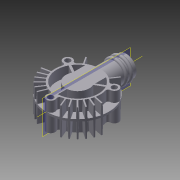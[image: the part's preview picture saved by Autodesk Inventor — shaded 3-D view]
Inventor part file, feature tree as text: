
AUTODESK INVENTOR PART (.ipt)
format: ipt  version: 2014 (Build 180170000, 170)  size: 2,437,632 bytes
history: native  units: in
note: dims shown in document units (in); Inventor stores cm internally (conversion verified against a paired STEP export)
features: sketch x24, extrude x21, pattern_circular x9, plane x4, draft x4, mirror x3, fillet x2, hole x2, revolve x2, other x1, thread x1
ambient origin geometry x8: Origin, YZ Plane, XZ Plane, XY Plane, X Axis, Y Axis, Z Axis, Center Point
bodies: Solid1 (feature_tree)
feature tree (73):
  extrude  "Extrusion1"  Depth=0.05in TaperAngle=0.0deg
  extrude  "Extrusion2"  Depth=1.08in
  extrude  "Extrusion3"  Depth=0.5in
  pattern_circular  "Circular Pattern1"  Count=3 Angle=360.0deg
  plane  "Work Plane2"
  extrude  "Extrusion17"  Depth=0.25in TaperAngle=0.0deg
  extrude  "Extrusion20"  Depth=0.25in
  draft  "FaceDraft5"
  draft  "FaceDraft6"
  fillet  "Fillet6"  Radius=0.125in
  pattern_circular  "Circular Pattern7"  Count=3 Angle=360.0deg
  extrude  "Extrusion21"  Depth=0.25in TaperAngle=360.0deg
  pattern_circular  "Circular Pattern8"  [2 undecoded]
  extrude  "Extrusion22"  Depth=0.25in
  draft  "FaceDraft7"
  draft  "FaceDraft8"
  fillet  "Fillet7"  Radius=0.125in
  pattern_circular  "Circular Pattern9"  [2 undecoded]
  extrude  "Extrusion23"  Depth=0.25in
  pattern_circular  "Circular Pattern10"  [2 undecoded]
  hole  "Hole1"  [1 undecoded]
  pattern_circular  "Circular Pattern11"  [2 undecoded]
  extrude  "Extrusion24"  Depth=0.25in
  plane  "Work Plane5"
  extrude  "Extrusion25"  Depth=0.25in TaperAngle=0.0deg
  hole  "Hole2"  [1 undecoded]
  other  "Work Axis1"
  revolve  "Revolution2"  [1 undecoded]
  pattern_circular  "Circular Pattern2"  [2 undecoded]
  extrude  "Extrusion5"  Depth=0.25in TaperAngle=360.0deg
  extrude  "Extrusion6"  Depth=0.25in
  mirror  "Mirror1"
  mirror  "Mirror2"
  extrude  "Extrusion7"  Depth=0.25in
  extrude  "Extrusion8"  Depth=0.25in TaperAngle=0.0deg
  extrude  "Extrusion9"  Depth=0.25in TaperAngle=360.0deg
  pattern_circular  "Circular Pattern3"  [2 undecoded]
  mirror  "Mirror3"
  extrude  "Extrusion10"  Depth=0.25in
  pattern_circular  "Circular Pattern4"  [2 undecoded]
  extrude  "Extrusion11"  Depth=0.25in
  plane  "Work Plane1"
  extrude  "Extrusion12"  Depth=0.25in TaperAngle=360.0deg
  extrude  "Extrusion13"  Depth=0.25in TaperAngle=0.0deg
  revolve  "Revolution1"  Angle=360.0deg
  extrude  "Extrusion14"  Depth=0.25in
  extrude  "Extrusion16"  Depth=0.25in TaperAngle=360.0deg
  thread  "Thread1"  [1 undecoded]
  sketch  "Sketch1"  dims[d0=1.5in d1=0.05in d2=0.0in]
  sketch  "Sketch2"  dims[d3=1.0in d4=1.08in]
  sketch  "Sketch3"  dims[d5=0.5625in d6=0.5in]
  sketch  "Sketch5"  dims[d7=0.25in d8=0.0in]
  sketch  "Sketch6"  dims[d9=0.05in]
  sketch  "Sketch7"  dims[d10=0.25in d11=0.0in d12=1.1811in d13=360.0deg]
  sketch  "Sketch8"  dims[d20=11.0236in d21=360.0deg d23=0.25in d24=0.0in]
  sketch  "Sketch9"  dims[d25=0.25in d26=0.0in d27=0.5in d28=0.125in d29=0.0in]
  sketch  "Sketch10"  dims[d30=1.0in]
  sketch  "Sketch11"  dims[d31=0.25in d32=0.0in]
  sketch  "Sketch12"  dims[d35=0.25in]
  sketch  "Sketch13"  dims[d36=0.2in]
  sketch  "Sketch14"  dims[d37=0.25in d38=0.0in d39=1.1811in d40=360.0deg]
  sketch  "Sketch15"  dims[d42=0.25in d43=0.0in d44=1.1811in d45=360.0deg]
  sketch  "Sketch17"  dims[d47=0.25in d48=0.0in]
  sketch  "Sketch18"  dims[d49=0.5in]
  sketch  "Sketch20"  dims[d50=0.0625in d51=0.625in d52=0.0in d53=0.0in]
  sketch  "Sketch21"  dims[d54=0.25in d55=0.0in]
  sketch  "Sketch22"  dims[d57=0.1in]
  sketch  "Sketch23"  dims[d58=0.1in]
  sketch  "Sketch24"  dims[d59=0.05in]
  plane  "Work Plane4"
  sketch  "Sketch26"  dims[d60=0.25in]
  sketch  "Sketch27"  dims[d61=0.5in]
  sketch  "Sketch28"  dims[d62=90.0deg d63=0.75in d64=0.0in d67=0.2in d68=0.125in d69=0.0in d70=1.0in d71=0.0in d72=0.25in d76=0.375in d77=0.0in d106=22.5deg d107=0.025in d108=0.025in d109=0.25in d110=0.0in d111=0.0137in d112=0.0137in d113=0.01in d114=12.5984in d115=360.0deg d117=0.1in d118=0.1in d119=0.25in d120=0.0in d121=1.1811in d122=360.0deg d124=0.25in d125=0.0in d126=0.0103in d127=0.0103in d128=0.01in d129=12.5984in d130=360.0deg d132=0.25in d133=0.0in d134=1.1811in d135=360.0deg d137=1.0in d138=1.0in d139=0.129in d140=0.75in d141=0.219in d142=0.112in d143=0.5635in d144=1.0in d145=0.8108in d146=1.1811in d147=360.0deg d149=0.125in d150=0.0in d152=-0.625in d153=0.5in d154=0.5625in d155=0.0in d156=0.313in d157=0.236in d158=0.0246in d159=0.329in d160=0.219in d161=0.112in d162=0.5635in d163=0.25in d164=0.8108in d165=0.125in d166=0.25in d167=90.0deg]
note: 18 required parameter values undecoded (feature->parameter linkage not recoverable at this tier; creation-order binding heuristic only, values carry confidence <= 0.55)